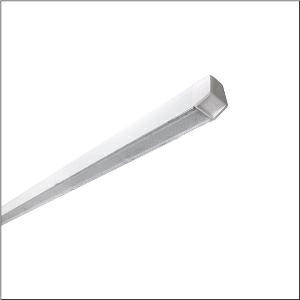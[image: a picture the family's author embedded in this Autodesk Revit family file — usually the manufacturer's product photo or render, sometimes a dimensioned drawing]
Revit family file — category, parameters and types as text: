
# Revit family: licross_r__11_recessed_ho_51ul1edv4m5r00s_7b8d
name_source: partatom
category: Lighting Fixtures
units: mm (PartAtom-declared; Revit-internal decimal feet)

## family parameters
Cut with Voids When Loaded = No
Host = Face
Light Source = No
Part Type = Normal
Room Calculation Point = No
Round Connector Dimension = Use Diameter
Shared = No

## types (1)
- --- (1 x LED, 25560 lm, 150.1 W, 4000K)
    Apparent Load = 150 VA
    CIE Flux Codes = 85 95 99 100 100
    Color Rendering = 80
    Color Temperature = 4000K
    Default Elevation = 1800 mm
    Description = Licross® 11 Recessed HO, single luminaire, primary optical cover: cover, of PMMA, light emission: direct distribution, primary light characteristic: symmetric, installation type: slip-in mounting, LED, rated luminous flux: 25.560lm, luminous efficacy: 170lm/W, light colour: 840, colour temperature: 4000K, control gear: ECG DALI, with terminal, 5-pole, max. 2.5mm², mains connection: 230V, AC, 50/60Hz, rated input power: 150W, Licross® LED insert, of sheet steel, galvanised, coil coated, white, with terminals, length: 2.327mm, width: 70mm, height: 71mm, end cap, of PC, white, mounting rail, of sheet steel, galvanised, white, protection rating (complete): IP20, insulation class (complete): insulation class I (protective earthing), certification: CE, ENEC, VDE, UKCA, impact resistance: IK06, permissible operating ambient temperature: -35..+35°C, corresponds to IFS (International Featured Standards) requirements for safety and quality in the food industry, reducing of maximum allowable ambient temperature of 5°C with ceiling mounting, LABS conformity tested according to VDMA 24364:2018-05, packaging unit: 1 piece
    Height = 58 mm
    Lamp = 1 x LED
    Lamp Light Flux = 25560 lm
    Lamp Power = 150.1 W
    Lamp count = 1
    Length = 2250 mm
    Luminous efficacy = 170 lm/W
    Manufacturer = Siteco
    ModVariant = No
    Model = 51UL1EDV4M5R00S
    Mounting Place = Ceiling
    Mounting Type = Pendant
    Number of Poles = 1
    OnlyDefault = Yes
    Power Factor = 1
    Product Name = Licross® 11 Recessed HO
    Product group = single luminaire
    ProductGroupID = 907
    Protection Class = Protection class I
    Protection Degree = IP 20
    RLX_Detail_Level = 1
    RLX_Emergency_Light_Flux = 0 lm
    RLX_Emergency_Type = 0
    RLX_Emergency_Type_DB = No
    RlxData = <blob elided: 32125 chars, md5=761b040b>
    Socket = socket
    Standby Power = 0 W
    System Light Flux = 25561 lm
    System Power = 150 W
    Type Comments = factory setting: luminous flux: 100 % | dim-lin: 254 | 575 mA
    Type Image = l_1006979.jpg
    URL = http://relux.com
    VarID = @adj_130763
    Voltage = 0 V
    Weight = 0.00 kg
    Width = 66 mm

## geometry (parser evidence)
native form markers: Blend x4, Sweep x9
no freeform markers — native parametric forms only
